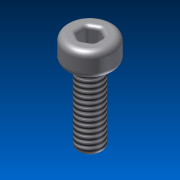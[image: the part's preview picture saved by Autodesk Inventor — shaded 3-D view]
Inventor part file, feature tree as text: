
AUTODESK INVENTOR PART (.ipt)
format: ipt  version: 2013 (Build 170138000, 138)  size: 176,640 bytes
history: native  units: mm
features: extrude x3, sketch x3, fillet x2, other x1, thread x1
ambient origin geometry x1: Origin
feature tree (10):
  other  "ソリッド1"
  extrude  "押し出し1"  Depth=3.8mm
  extrude  "押し出し2"  Depth=2.0mm TaperAngle=0.0deg
  extrude  "押し出し3"  Depth=2.0mm
  fillet  "フィレット1"  Radius=6.0mm
  fillet  "フィレット2"  Radius=0.75mm
  thread  "ねじ3"
  sketch  "スケッチ1"
  sketch  "スケッチ2"
  sketch  "スケッチ3"
